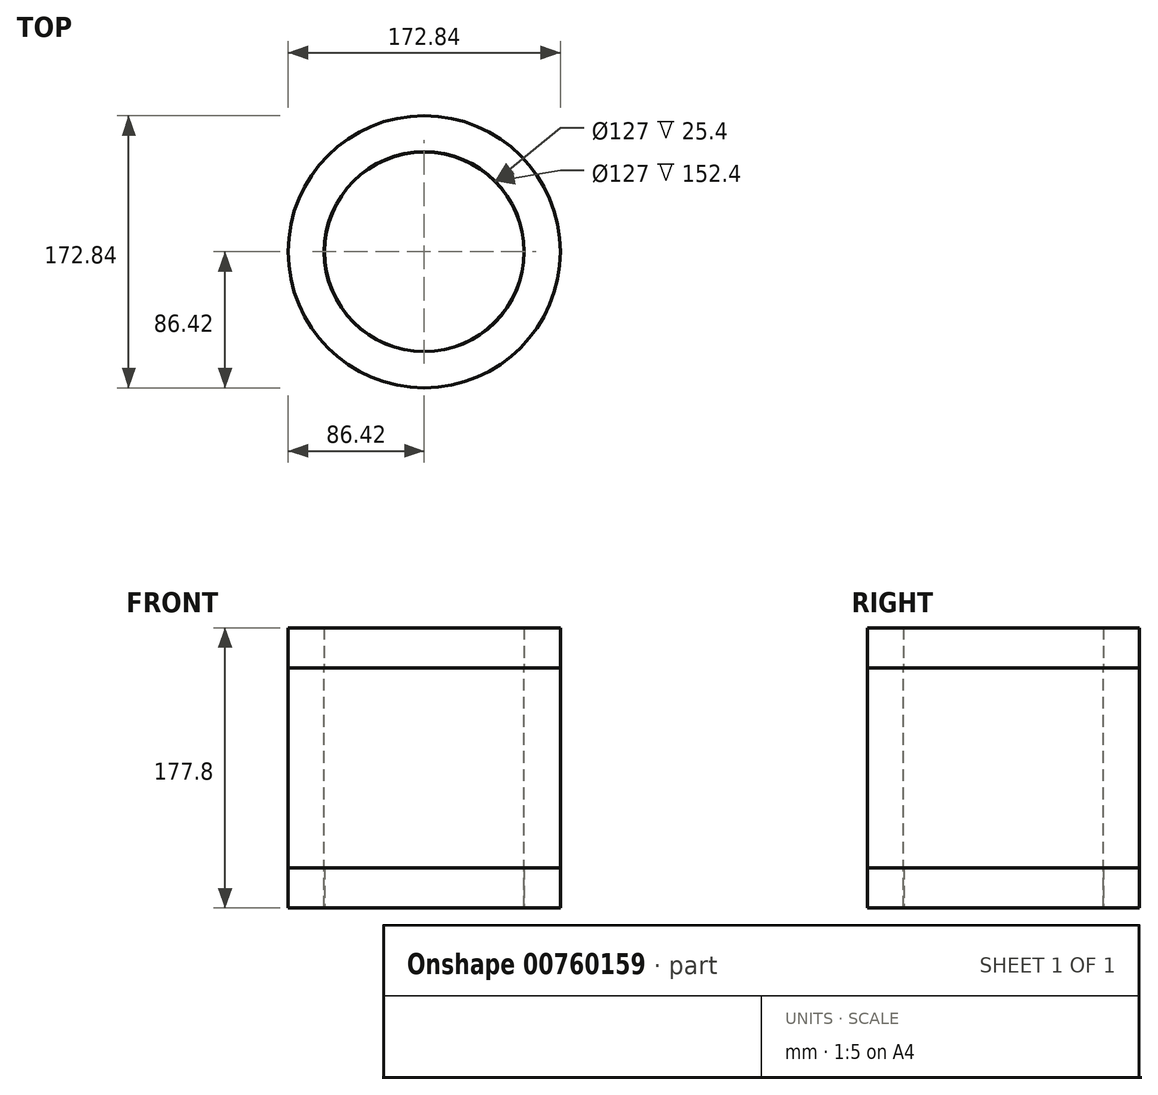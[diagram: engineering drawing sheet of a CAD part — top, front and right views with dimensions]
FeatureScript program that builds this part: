
annotation { "Feature Type Name" : "Feature", "Feature Type Description" : "" }
export const myFeature = defineFeature(function(context is Context, id is Id, definition is map)
    precondition{}
    {
        {
            var Q0;
            Q0=qCreatedBy(makeId("Top.planeOp"),FACE);
            var sketch = newSketch(context, id + "F0", { "sketchPlane" : qUnion([Q0])});
            skCircle(sketch, "E0", {"center": v(0, 0) * mm, "radius": 86.42 * mm});
            skSolve(sketch);
        }
        {
            var Q0;
            Q0 = qSketchRegion(id + "F0", true);
            extrude(context, id + "F1", {"entities" : qUnion([Q0]), "depth" : 152.4 * mm, "offsetDistance" : 25.4 * mm});
        }
        {
            var Q0;
            Q0=makeQuery(id+"F1.opExtrude","CAP_FACE",FACE,{"disambiguationData":[OSD([sQuery(id+"F0.wireOp",EDGE,"E0")])],"isStart":false});
            var sketch = newSketch(context, id + "F2", { "sketchPlane" : qUnion([Q0])});
            skCircle(sketch, "E1", {"center": v(0, 0) * mm, "radius": 69.9 * mm});
            skSolve(sketch);
        }
        {
            var Q0;
            Q0=sQuery(id+"F2.wireOp",VERTEX,"E1.center");
            var Q1;
            Q1=makeQuery(id+"F1.opExtrude","SWEPT_BODY",BODY,{"disambiguationData":[OSD([sQuery(id+"F0.wireOp",EDGE,"E0")])]});
            hole(context, id + "F3", {"style" : HoleStyle.SIMPLE, "endStyle" : HoleEndStyle.THROUGH, "holeDiameter" : 127 * mm, "majorDiameter" : 6.35 * mm, "isTappedThrough" : true, "tappedDepth" : 12.7 * mm, "tapClearance" : 3, "locations" : qUnion([Q0]), "scope" : qUnion([Q1])});
        }
        {
            var Q0;
            Q0=qCreatedBy(makeId("Top.planeOp"),FACE);
            var sketch = newSketch(context, id + "F4", { "sketchPlane" : qUnion([Q0])});
            skCircle(sketch, "E2", {"center": v(0, 0) * mm, "radius": 62.88 * mm});
            skCircle(sketch, "E3", {"center": v(0, 0) * mm, "radius": 67.7 * mm});
            skSolve(sketch);
        }
        {
            var Q0;
            Q0=sQuery(id+"F4.wireOp",EDGE,"E3");
            extrude(context, id + "F5", {"bodyType" : ToolBodyType.SURFACE, "surfaceEntities" : qUnion([Q0]), "depth" : 19.05 * mm, "offsetDistance" : 25.4 * mm});
        }
        {
            var Q0;
            Q0=qCreatedBy(makeId("Top.planeOp"),FACE);
            var sketch = newSketch(context, id + "F6", { "sketchPlane" : qUnion([Q0])});
            skCircle(sketch, "E4", {"center": v(0, 0) * mm, "radius": 63.34 * mm});
            skCircle(sketch, "E5", {"center": v(0, 0) * mm, "radius": 64.1 * mm});
            skSolve(sketch);
        }
        {
            var Q0;
            Q0=makeQuery(id+"F6.imprint","IMPRINT",FACE,{"disambiguationData":[TD([[makeQuery(id+"F6.imprint","IMPRINT",EDGE,{"derivedFrom":sQuery(id+"F6.wireOp",EDGE,"E4")}),1.0]])]});
            var Q1;
            Q1=makeQuery(id+"F1.opExtrude","CAP_FACE",FACE,{"disambiguationData":[OSD([sQuery(id+"F0.wireOp",EDGE,"E0")])],"isStart":false});
            var Q2;
            Q2 = qSketchRegion(id + "F0", true);
            var Q3;
            Q3=sQuery(id+"F6.wireOp",EDGE,"E5");
            var Q4;
            Q4=sQuery(id+"F6.wireOp",EDGE,"E4");
            extrude(context, id + "F7", {"entities" : qUnion([Q0, Q1, Q2]), "surfaceEntities" : qUnion([Q3, Q4]), "depth" : 25.4 * mm, "offsetDistance" : 25.4 * mm});
        }
    });
